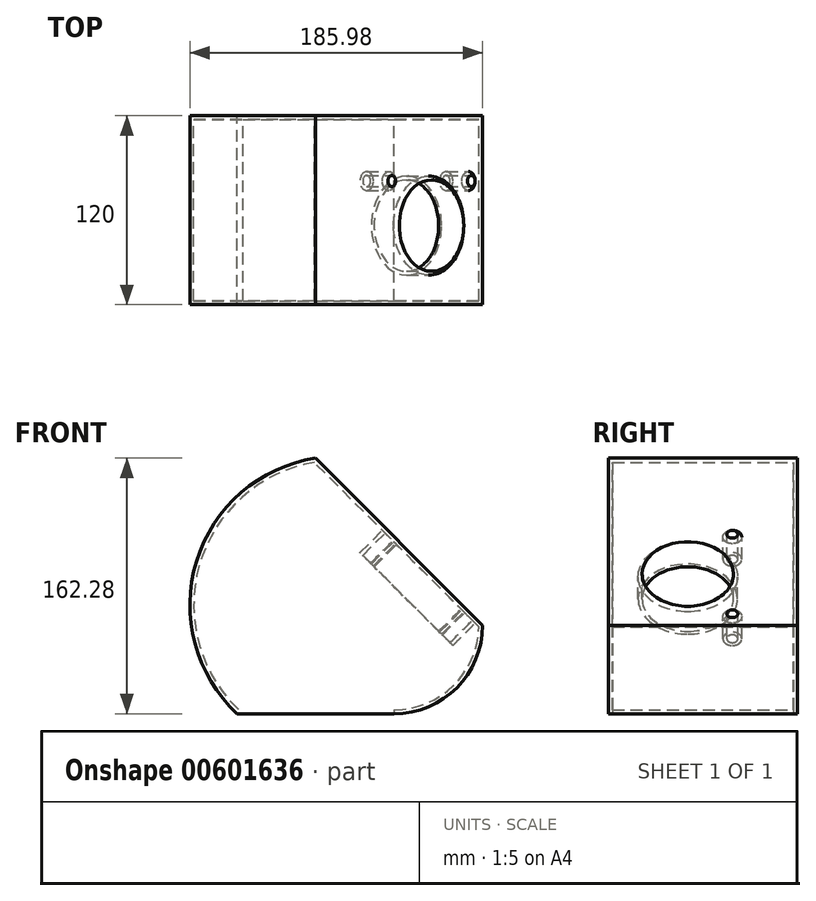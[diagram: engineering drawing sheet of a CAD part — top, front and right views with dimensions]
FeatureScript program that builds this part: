
annotation { "Feature Type Name" : "Feature", "Feature Type Description" : "" }
export const myFeature = defineFeature(function(context is Context, id is Id, definition is map)
    precondition{}
    {
        {
            var Q0;
            Q0=qCreatedBy(makeId("Front.planeOp"),FACE);
            var sketch = newSketch(context, id + "F0", { "sketchPlane" : qUnion([Q0])});
            skLineSegment(sketch, "E0", {"start": v(121.24, 56.22) * mm, "end": v(15.18, 162.28) * mm});
            skLineSegment(sketch, "E1", {"start": v(-34.67, 0) * mm, "end": v(65.03, 0) * mm});
            skArc(sketch, "E2", {"start": v(15.18, 162.28) * mm, "mid": v(-60.58, 96.76) * mm, "end": v(-34.67, 0) * mm});
            skArc(sketch, "E3", {"start": v(65.03, 0) * mm, "mid": v(104.78, 16.47) * mm, "end": v(121.24, 56.22) * mm});
            skSolve(sketch);
        }
        {
            var Q0;
            Q0=makeQuery(id+"F0.imprint","IMPRINT",FACE,{"disambiguationData":[TD([[makeQuery(id+"F0.imprint","IMPRINT",EDGE,{"derivedFrom":sQuery(id+"F0.wireOp",EDGE,"E0")}),1.0]])]});
            extrude(context, id + "F1", {"entities" : qUnion([Q0]), "endBound" : BoundingType.SYMMETRIC, "depth" : 120 * mm});
        }
        {
            var Q0;
            Q0=makeQuery(id+"F1.opExtrude","SWEPT_FACE",FACE,{"disambiguationData":[OSD([sQuery(id+"F0.wireOp",EDGE,"E0")])]});
            var sketch = newSketch(context, id + "F2", { "sketchPlane" : qUnion([Q0])});
            skLineSegment(sketch, "E4.bottom", {"start": v(24.06, 43.2) * mm, "end": v(-80.44, 43.2) * mm});
            skLineSegment(sketch, "E4.top", {"start": v(24.06, -43.2) * mm, "end": v(-80.44, -43.2) * mm});
            skLineSegment(sketch, "E4.left", {"start": v(26.06, 41.2) * mm, "end": v(26.06, -41.2) * mm});
            skLineSegment(sketch, "E4.right", {"start": v(-82.44, 41.2) * mm, "end": v(-82.44, -41.2) * mm});
            skPoint(sketch, "E4.middle", {"position": v(-28.19, 0) * mm});
            skPoint(sketch, "E5.visualSharp", {"position": v(-82.44, -43.2) * mm});
            skArc(sketch, "E5.filletArc", {"start": v(-82.44, -41.2) * mm, "mid": v(-81.85, -42.61) * mm, "end": v(-80.44, -43.2) * mm});
            skPoint(sketch, "E6.visualSharp", {"position": v(-82.44, 43.2) * mm});
            skArc(sketch, "E6.filletArc", {"start": v(-80.44, 43.2) * mm, "mid": v(-81.85, 42.61) * mm, "end": v(-82.44, 41.2) * mm});
            skPoint(sketch, "E7.visualSharp", {"position": v(26.06, 43.2) * mm});
            skArc(sketch, "E7.filletArc", {"start": v(26.06, 41.2) * mm, "mid": v(25.48, 42.61) * mm, "end": v(24.06, 43.2) * mm});
            skPoint(sketch, "E8.visualSharp", {"position": v(26.06, -43.2) * mm});
            skArc(sketch, "E8.filletArc", {"start": v(24.06, -43.2) * mm, "mid": v(25.48, -42.61) * mm, "end": v(26.06, -41.2) * mm});
            skCircle(sketch, "E9", {"center": v(-9.74, 0) * mm, "radius": 29 * mm});
            skCircle(sketch, "E10", {"center": v(-74.94, -35.7) * mm, "radius": 3.5 * mm});
            skCircle(sketch, "E11", {"center": v(-74.94, 35.7) * mm, "radius": 3.5 * mm});
            skCircle(sketch, "E12", {"center": v(18.56, 35.7) * mm, "radius": 3.5 * mm});
            skCircle(sketch, "E13", {"center": v(18.56, -35.7) * mm, "radius": 3.5 * mm});
            skSolve(sketch);
        }
        {
            var Q0;
            Q0=makeQuery(id+"F2.imprint","IMPRINT",FACE,{"disambiguationData":[TD([[makeQuery(id+"F2.imprint","IMPRINT",EDGE,{"derivedFrom":sQuery(id+"F2.wireOp",EDGE,"E4.bottom")}),1.0]])]});
            var Q1;
            Q1=makeQuery(id+"F2.imprint","IMPRINT",FACE,{"disambiguationData":[TD([[makeQuery(id+"F2.imprint","IMPRINT",EDGE,{"derivedFrom":sQuery(id+"F2.wireOp",EDGE,"E9")}),1.0]])]});
            var Q2;
            Q2=makeQuery(id+"F2.imprint","IMPRINT",FACE,{"disambiguationData":[TD([[makeQuery(id+"F2.imprint","IMPRINT",EDGE,{"derivedFrom":sQuery(id+"F2.wireOp",EDGE,"E10")}),1.0]])]});
            var Q3;
            Q3=makeQuery(id+"F2.imprint","IMPRINT",FACE,{"disambiguationData":[TD([[makeQuery(id+"F2.imprint","IMPRINT",EDGE,{"derivedFrom":sQuery(id+"F2.wireOp",EDGE,"E11")}),1.0]])]});
            var Q4;
            Q4=makeQuery(id+"F2.imprint","IMPRINT",FACE,{"disambiguationData":[TD([[makeQuery(id+"F2.imprint","IMPRINT",EDGE,{"derivedFrom":sQuery(id+"F2.wireOp",EDGE,"E12")}),1.0]])]});
            var Q5;
            Q5=makeQuery(id+"F2.imprint","IMPRINT",FACE,{"disambiguationData":[TD([[makeQuery(id+"F2.imprint","IMPRINT",EDGE,{"derivedFrom":sQuery(id+"F2.wireOp",EDGE,"E13")}),1.0]])]});
            extrude(context, id + "F3", {"entities" : qUnion([Q0, Q1, Q2, Q3, Q4, Q5]), "operationType" : NewBodyOperationType.REMOVE, "oppositeDirection" : true, "depth" : 20 * mm});
        }
        {
            var Q0;
            Q0=makeQuery(id+"F1.opExtrude","SWEPT_FACE",FACE,{"disambiguationData":[OSD([sQuery(id+"F0.wireOp",EDGE,"E1")])]});
            shell(context, id + "F4", {"entities" : qUnion([Q0]), "thickness" : 2.5 * mm});
        }
        {
            var Q0;
            Q0=makeQuery(id+"F2.imprint","IMPRINT",FACE,{"disambiguationData":[TD([[makeQuery(id+"F2.imprint","IMPRINT",EDGE,{"derivedFrom":sQuery(id+"F2.wireOp",EDGE,"E9")}),1.0]])]});
            var Q1;
            Q1=makeQuery(id+"F2.imprint","IMPRINT",FACE,{"disambiguationData":[TD([[makeQuery(id+"F2.imprint","IMPRINT",EDGE,{"derivedFrom":sQuery(id+"F2.wireOp",EDGE,"E11")}),1.0]])]});
            var Q2;
            Q2=makeQuery(id+"F2.imprint","IMPRINT",FACE,{"disambiguationData":[TD([[makeQuery(id+"F2.imprint","IMPRINT",EDGE,{"derivedFrom":sQuery(id+"F2.wireOp",EDGE,"E10")}),1.0]])]});
            var Q3;
            Q3=makeQuery(id+"F2.imprint","IMPRINT",FACE,{"disambiguationData":[TD([[makeQuery(id+"F2.imprint","IMPRINT",EDGE,{"derivedFrom":sQuery(id+"F2.wireOp",EDGE,"E13")}),1.0]])]});
            var Q4;
            Q4=makeQuery(id+"F2.imprint","IMPRINT",FACE,{"disambiguationData":[TD([[makeQuery(id+"F2.imprint","IMPRINT",EDGE,{"derivedFrom":sQuery(id+"F2.wireOp",EDGE,"E12")}),1.0]])]});
            extrude(context, id + "F5", {"entities" : qUnion([Q0, Q1, Q2, Q3, Q4]), "operationType" : NewBodyOperationType.REMOVE, "oppositeDirection" : true, "depth" : 40 * mm});
        }
    });
